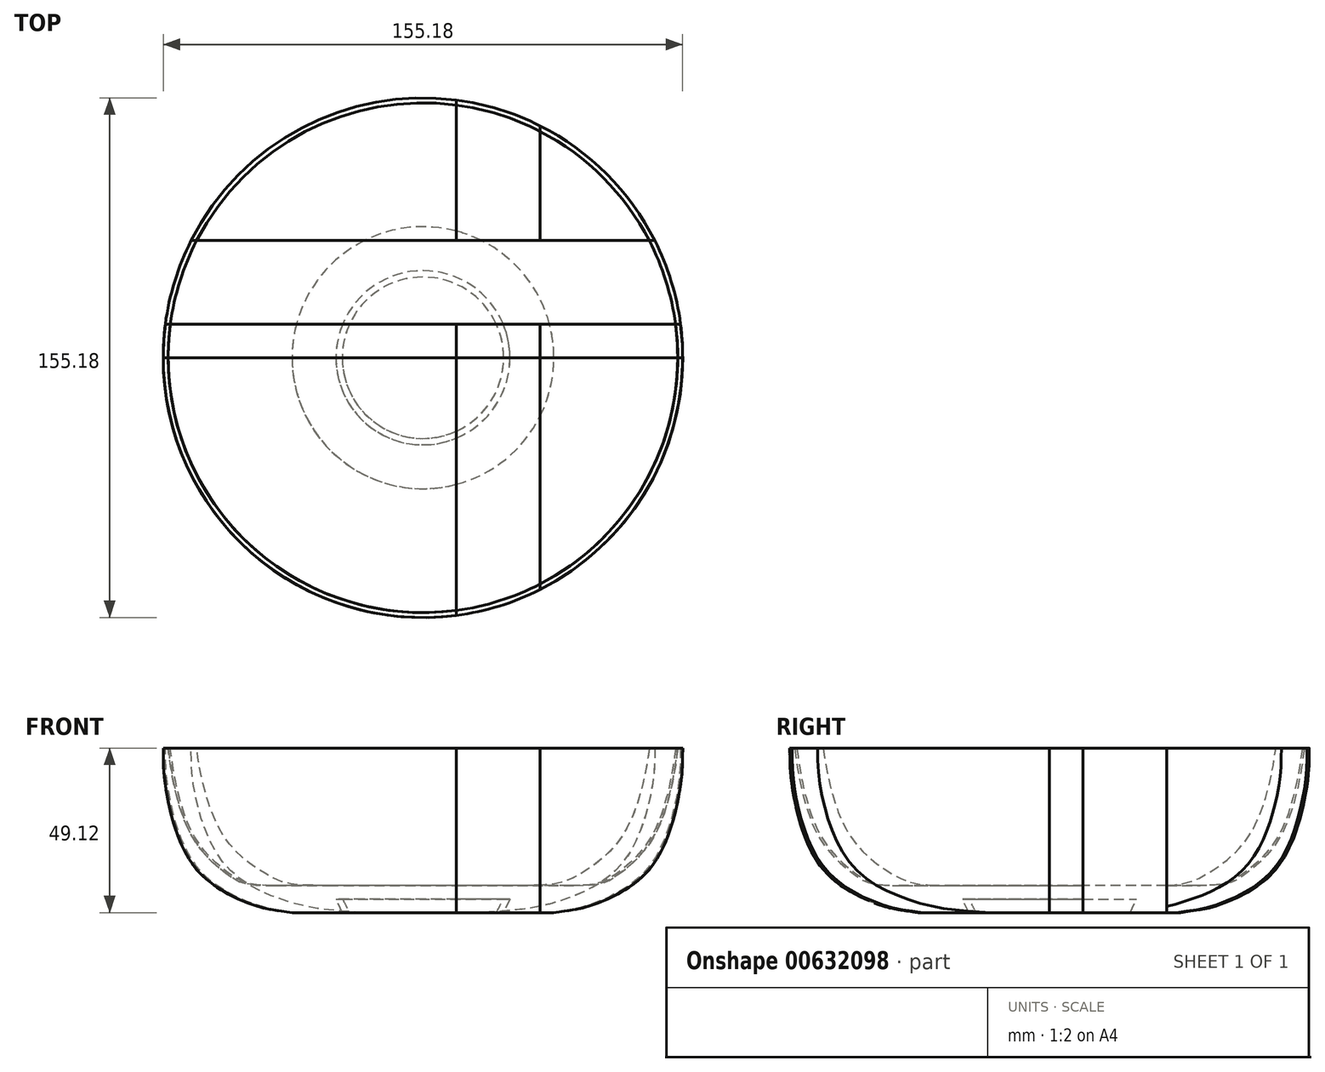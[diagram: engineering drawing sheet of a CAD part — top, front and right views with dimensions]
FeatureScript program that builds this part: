
annotation { "Feature Type Name" : "Feature", "Feature Type Description" : "" }
export const myFeature = defineFeature(function(context is Context, id is Id, definition is map)
    precondition{}
    {
        {
            var Q0;
            Q0=qCreatedBy(makeId("Top.planeOp"),FACE);
            var sketch = newSketch(context, id + "F0", { "sketchPlane" : qUnion([Q0])});
            skLineSegment(sketch, "E0.bottom", {"start": v(0, 0) * mm, "end": v(90, 0) * mm});
            skLineSegment(sketch, "E0.top", {"start": v(0, 25) * mm, "end": v(90, 25) * mm});
            skLineSegment(sketch, "E0.left", {"start": v(0, 0) * mm, "end": v(0, 25) * mm});
            skLineSegment(sketch, "E1.bottom", {"start": v(90, 25) * mm, "end": v(115, 25) * mm});
            skLineSegment(sketch, "E1.top", {"start": v(100, 0) * mm, "end": v(115, 0) * mm});
            skLineSegment(sketch, "E2.bottom", {"start": v(115, 25) * mm, "end": v(160, 25) * mm});
            skLineSegment(sketch, "E2.top", {"start": v(125, 0) * mm, "end": v(160, 0) * mm});
            skLineSegment(sketch, "E2.right", {"start": v(160, 25) * mm, "end": v(160, 0) * mm});
            skLineSegment(sketch, "E3.top", {"start": v(0, 70) * mm, "end": v(90, 70) * mm});
            skLineSegment(sketch, "E3.left", {"start": v(0, 25) * mm, "end": v(0, 70) * mm});
            skLineSegment(sketch, "E3.right", {"start": v(90, 25) * mm, "end": v(90, 70) * mm});
            skLineSegment(sketch, "E4.bottom", {"start": v(90, 70) * mm, "end": v(115, 70) * mm});
            skLineSegment(sketch, "E4.left", {"start": v(90, 70) * mm, "end": v(90, 25) * mm});
            skLineSegment(sketch, "E4.right", {"start": v(115, 70) * mm, "end": v(115, 25) * mm});
            skLineSegment(sketch, "E5.bottom", {"start": v(115, 70) * mm, "end": v(160, 70) * mm});
            skLineSegment(sketch, "E5.right", {"start": v(160, 70) * mm, "end": v(160, 25) * mm});
            skLineSegment(sketch, "E6.top", {"start": v(0, -90) * mm, "end": v(90, -90) * mm});
            skLineSegment(sketch, "E6.left", {"start": v(0, 0) * mm, "end": v(0, -90) * mm});
            skLineSegment(sketch, "E6.right", {"start": v(90, 0) * mm, "end": v(90, -90) * mm});
            skLineSegment(sketch, "E7.bottom", {"start": v(90, 0) * mm, "end": v(115, 0) * mm});
            skLineSegment(sketch, "E7.top", {"start": v(90, -90) * mm, "end": v(115, -90) * mm});
            skLineSegment(sketch, "E7.right", {"start": v(115, 0) * mm, "end": v(115, -90) * mm});
            skLineSegment(sketch, "E8.bottom", {"start": v(115, 0) * mm, "end": v(160, 0) * mm});
            skLineSegment(sketch, "E8.top", {"start": v(115, -90) * mm, "end": v(160, -90) * mm});
            skLineSegment(sketch, "E8.right", {"start": v(160, 0) * mm, "end": v(160, -90) * mm});
            skLineSegment(sketch, "E9", {"start": v(0, -10) * mm, "end": v(160, -10) * mm});
            skLineSegment(sketch, "E10", {"start": v(80, -99.76) * mm, "end": v(80, 101.9) * mm, "construction": true});
            skSolve(sketch);
        }
        {
            var Q0;
            Q0=makeQuery(id+"F0.imprint","IMPRINT",FACE,{"disambiguationData":[TD([[makeQuery(id+"F0.imprint","IMPRINT",EDGE,{"derivedFrom":sQuery(id+"F0.wireOp",EDGE,"E0.top")}),1.0]])]});
            extrude(context, id + "F1", {"entities" : qUnion([Q0]), "depth" : 50 * mm, "offsetDistance" : 25 * mm});
        }
        {
            var Q0;
            Q0=makeQuery(id+"F0.imprint","IMPRINT",FACE,{"disambiguationData":[TD([[makeQuery(id+"F0.imprint","IMPRINT",EDGE,{"derivedFrom":sQuery(id+"F0.wireOp",EDGE,"E4.bottom")}),-1.0]])]});
            extrude(context, id + "F2", {"entities" : qUnion([Q0]), "depth" : 50 * mm, "offsetDistance" : 25 * mm});
        }
        {
            var Q0;
            Q0=makeQuery(id+"F0.imprint","IMPRINT",FACE,{"disambiguationData":[TD([[makeQuery(id+"F0.imprint","IMPRINT",EDGE,{"derivedFrom":sQuery(id+"F0.wireOp",EDGE,"E5.bottom")}),-1.0]])]});
            extrude(context, id + "F3", {"entities" : qUnion([Q0]), "depth" : 50 * mm, "offsetDistance" : 25 * mm});
        }
        {
            var Q0;
            Q0=makeQuery(id+"F0.imprint","IMPRINT",FACE,{"disambiguationData":[TD([[makeQuery(id+"F0.imprint","IMPRINT",EDGE,{"derivedFrom":sQuery(id+"F0.wireOp",EDGE,"E0.left")}),-1.0]])]});
            extrude(context, id + "F4", {"entities" : qUnion([Q0]), "depth" : 50 * mm, "offsetDistance" : 25 * mm});
        }
        {
            var Q0;
            Q0=makeQuery(id+"F0.imprint","IMPRINT",FACE,{"disambiguationData":[TD([[makeQuery(id+"F0.imprint","IMPRINT",EDGE,{"derivedFrom":sQuery(id+"F0.wireOp",EDGE,"E1.left")}),1.0]])]});
            var Q1;
            {var subQ0=sQuery(id+"F0.wireOp",EDGE,"E0.bottom");Q1=makeQuery(id+"F0.imprint","IMPRINT",FACE,{"disambiguationData":[TD([[makeQuery(id+"F0.imprint","IMPRINT",EDGE,{"derivedFrom":subQ0}),-1.0]])]});}
            var Q2;
            {var subQ0=sQuery(id+"F0.wireOp",EDGE,"E8.bottom");Q2=makeQuery(id+"F0.imprint","IMPRINT",FACE,{"disambiguationData":[TD([[makeQuery(id+"F0.imprint","IMPRINT",EDGE,{"derivedFrom":subQ0}),-1.0]])]});}
            var Q3;
            {var subQ0=sQuery(id+"F0.wireOp",EDGE,"E6.top");Q3=makeQuery(id+"F0.imprint","IMPRINT",FACE,{"disambiguationData":[TD([[makeQuery(id+"F0.imprint","IMPRINT",EDGE,{"derivedFrom":subQ0}),1.0]])]});}
            var Q4;
            {var subQ0=sQuery(id+"F0.wireOp",EDGE,"E8.top");Q4=makeQuery(id+"F0.imprint","IMPRINT",FACE,{"disambiguationData":[TD([[makeQuery(id+"F0.imprint","IMPRINT",EDGE,{"derivedFrom":subQ0}),1.0]])]});}
            extrude(context, id + "F5", {"entities" : qUnion([Q0, Q1, Q2, Q3, Q4]), "depth" : 50 * mm, "offsetDistance" : 25 * mm});
        }
        {
            var Q0;
            {var subQ0=sQuery(id+"F0.wireOp",EDGE,"E7.bottom");Q0=makeQuery(id+"F0.imprint","IMPRINT",FACE,{"disambiguationData":[TD([[makeQuery(id+"F0.imprint","IMPRINT",EDGE,{"derivedFrom":subQ0}),-1.0]])]});}
            var Q1;
            {var subQ0=sQuery(id+"F0.wireOp",EDGE,"E7.top");Q1=makeQuery(id+"F0.imprint","IMPRINT",FACE,{"disambiguationData":[TD([[makeQuery(id+"F0.imprint","IMPRINT",EDGE,{"derivedFrom":subQ0}),1.0]])]});}
            extrude(context, id + "F6", {"entities" : qUnion([Q0, Q1]), "depth" : 50 * mm, "offsetDistance" : 25 * mm});
        }
        {
            var Q0;
            {var subQ0=sQuery(id+"F0.wireOp",EDGE,"E0.bottom");Q0=makeQuery(id+"F0.imprint","IMPRINT",FACE,{"disambiguationData":[TD([[makeQuery(id+"F0.imprint","IMPRINT",EDGE,{"derivedFrom":subQ0}),-1.0]])]});}
            extrude(context, id + "F7", {"entities" : qUnion([Q0]), "depth" : 50 * mm, "offsetDistance" : 25 * mm});
        }
        {
            var Q0;
            {var subQ0=sQuery(id+"F0.wireOp",EDGE,"E7.bottom");Q0=makeQuery(id+"F0.imprint","IMPRINT",FACE,{"disambiguationData":[TD([[makeQuery(id+"F0.imprint","IMPRINT",EDGE,{"derivedFrom":subQ0}),-1.0]])]});}
            extrude(context, id + "F8", {"entities" : qUnion([Q0]), "depth" : 50 * mm, "offsetDistance" : 25 * mm});
        }
        {
            var Q0;
            {var subQ0=sQuery(id+"F0.wireOp",EDGE,"E8.bottom");Q0=makeQuery(id+"F0.imprint","IMPRINT",FACE,{"disambiguationData":[TD([[makeQuery(id+"F0.imprint","IMPRINT",EDGE,{"derivedFrom":subQ0}),-1.0]])]});}
            extrude(context, id + "F9", {"entities" : qUnion([Q0]), "depth" : 50 * mm, "offsetDistance" : 25 * mm});
        }
        {
            var Q0;
            {var subQ0=sQuery(id+"F0.wireOp",EDGE,"E6.top");Q0=makeQuery(id+"F0.imprint","IMPRINT",FACE,{"disambiguationData":[TD([[makeQuery(id+"F0.imprint","IMPRINT",EDGE,{"derivedFrom":subQ0}),1.0]])]});}
            extrude(context, id + "F10", {"entities" : qUnion([Q0]), "depth" : 50 * mm, "offsetDistance" : 25 * mm});
        }
        {
            var Q0;
            {var subQ0=sQuery(id+"F0.wireOp",EDGE,"E7.top");Q0=makeQuery(id+"F0.imprint","IMPRINT",FACE,{"disambiguationData":[TD([[makeQuery(id+"F0.imprint","IMPRINT",EDGE,{"derivedFrom":subQ0}),1.0]])]});}
            extrude(context, id + "F11", {"entities" : qUnion([Q0]), "depth" : 50 * mm, "offsetDistance" : 25 * mm});
        }
        {
            var Q0;
            {var subQ0=sQuery(id+"F0.wireOp",EDGE,"E8.top");Q0=makeQuery(id+"F0.imprint","IMPRINT",FACE,{"disambiguationData":[TD([[makeQuery(id+"F0.imprint","IMPRINT",EDGE,{"derivedFrom":subQ0}),1.0]])]});}
            extrude(context, id + "F12", {"entities" : qUnion([Q0]), "depth" : 50 * mm, "offsetDistance" : 25 * mm});
        }
        {
            var Q0;
            Q0=makeQuery(id+"F7.opExtrude","SWEPT_FACE",FACE,{"disambiguationData":[OSD([sQuery(id+"F0.wireOp",EDGE,"E9")])]});
            var sketch = newSketch(context, id + "F13", { "sketchPlane" : qUnion([Q0])});
            skLineSegment(sketch, "E11", {"start": v(80, 72.12) * mm, "end": v(80, -27.18) * mm, "construction": true});
            skLineSegment(sketch, "E12", {"start": v(80, 4) * mm, "end": v(106, 4) * mm});
            skLineSegment(sketch, "E13", {"start": v(106, 4) * mm, "end": v(104.1, 0) * mm});
            skLineSegment(sketch, "E14", {"start": v(104.1, 0) * mm, "end": v(119.1, 0) * mm});
            skLineSegment(sketch, "E15", {"start": v(80, 8.1) * mm, "end": v(125, 8.1) * mm});
            skFitSpline(sketch, "E16", {"points": [v(125, 8.1) * mm, v(137.42, 10.74) * mm, v(148.74, 22.34) * mm, v(156.11, 49) * mm], "startDerivative": vector(87.08, 0) * mm, "endDerivative": vector(7.06, 60.03) * mm});
            skLineSegment(sketch, "E17", {"start": v(156.11, 49) * mm, "end": v(157.6, 49.12) * mm});
            skLineSegment(sketch, "E18", {"start": v(80, 8.1) * mm, "end": v(80, 4) * mm});
            skFitSpline(sketch, "E19", {"points": [v(119.1, 0) * mm, v(132.7, 3.03) * mm, v(148.24, 13.65) * mm, v(156.75, 36.8) * mm, v(157.6, 49.12) * mm], "startDerivative": vector(102.12, 13.3) * mm, "endDerivative": vector(0.04, 70.37) * mm});
            skSolve(sketch);
        }
        {
            var Q0;
            {var subQ0=sQuery(id+"F13.wireOp",EDGE,"E18");Q0=makeQuery(id+"F13.imprint","IMPRINT",FACE,{"disambiguationData":[TD([[makeQuery(id+"F13.imprint","IMPRINT",EDGE,{"derivedFrom":subQ0}),1.0]])]});}
            var Q1;
            {var subQ3=sQuery(id+"F13.wireOp",EDGE,"f76ab763-0c6e-4cc8-a736-abfbcbe2b951");Q1=makeQuery(id+"F13.imprint","IMPRINT",FACE,{"disambiguationData":[TD([[makeQuery(id+"F13.imprint","IMPRINT",EDGE,{"derivedFrom":subQ3}),1.0]])]});}
            var Q2;
            {var subQ0=sQuery(id+"F13.wireOp",EDGE,"E14");var subQ1=sQuery(id+"F13.wireOp",EDGE,"E13");var subQ2=sQuery(id+"F0.wireOp",EDGE,"E9");var subQ3=makeQuery(id+"F13.imprint","INTERSECT",VERTEX,{"derivedFrom":[makeQuery(id+"F7.opExtrude","CAP_EDGE",EDGE,{"disambiguationData":[OSD([subQ2])],"isStart":true}),subQ1,subQ0]});Q2=makeQuery(id+"F13.imprint","IMPRINT",FACE,{"disambiguationData":[TD([[makeQuery(id+"F13.imprint","IMPRINT",EDGE,{"disambiguationData":[TD([[subQ3,1.0]])],"derivedFrom":subQ1}),1.0]])]});}
            var Q3;
            Q3=sQuery(id+"F13.wireOp",EDGE,"E11");
            revolve(context, id + "F14", {"operationType" : NewBodyOperationType.INTERSECT, "entities" : qUnion([Q0, Q1, Q2]), "axis" : qUnion([Q3]), "revolveType" : RevolveType.FULL, "oppositeDirection" : true});
        }
    });
